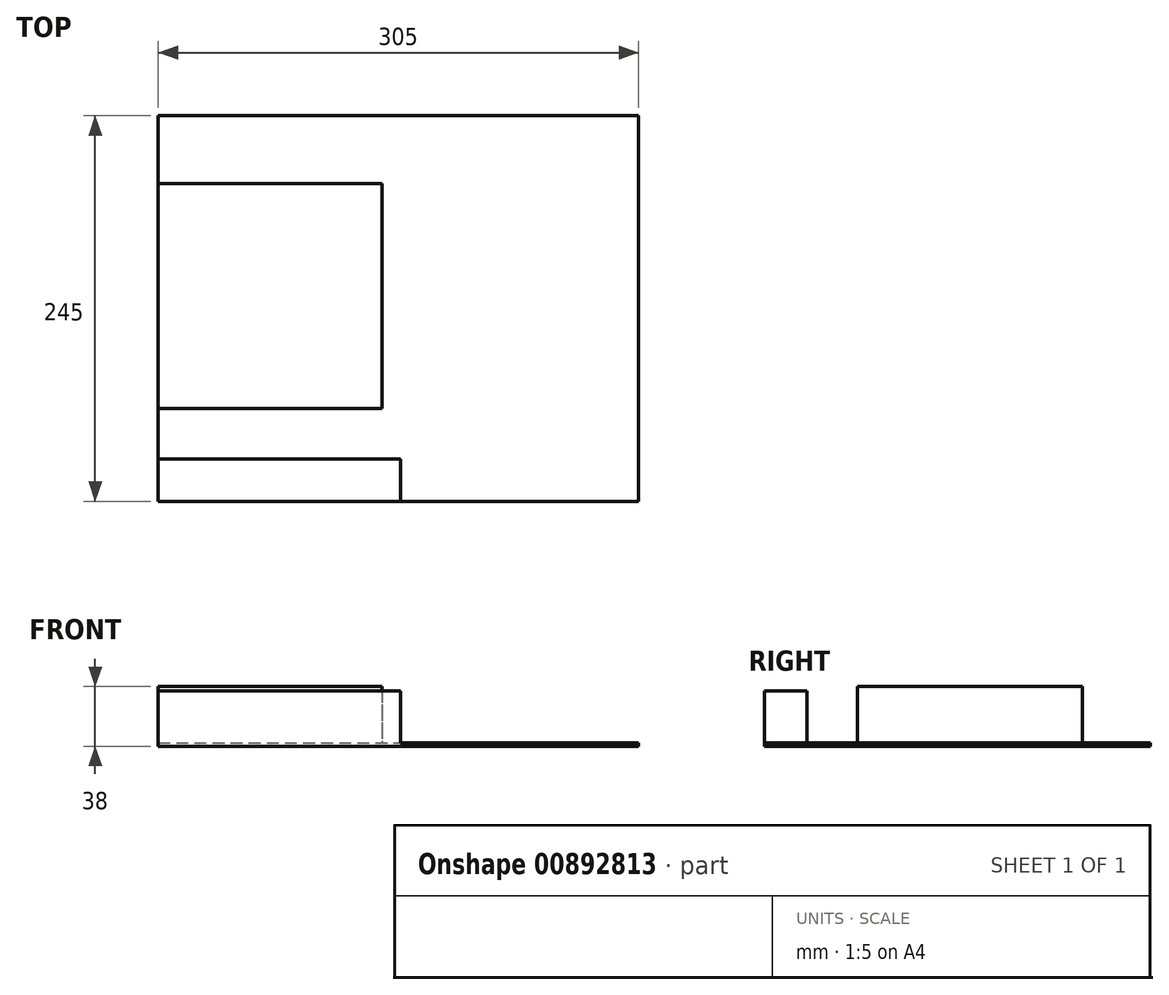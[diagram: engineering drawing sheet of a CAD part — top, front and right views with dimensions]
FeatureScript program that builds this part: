
annotation { "Feature Type Name" : "Feature", "Feature Type Description" : "" }
export const myFeature = defineFeature(function(context is Context, id is Id, definition is map)
    precondition{}
    {
        {
            var Q0;
            Q0=qCreatedBy(makeId("Top.planeOp"),FACE);
            var sketch = newSketch(context, id + "F0", { "sketchPlane" : qUnion([Q0])});
            skLineSegment(sketch, "E0.bottom", {"start": v(-152.5, 122.5) * mm, "end": v(152.5, 122.5) * mm});
            skLineSegment(sketch, "E0.top", {"start": v(-152.5, -122.5) * mm, "end": v(152.5, -122.5) * mm});
            skLineSegment(sketch, "E0.left", {"start": v(-152.5, 122.5) * mm, "end": v(-152.5, -122.5) * mm});
            skLineSegment(sketch, "E0.right", {"start": v(152.5, 122.5) * mm, "end": v(152.5, -122.5) * mm});
            skLineSegment(sketch, "E1", {"start": v(0, 146.94) * mm, "end": v(0, -146.94) * mm, "construction": true});
            skLineSegment(sketch, "E2", {"start": v(-203.7, 0) * mm, "end": v(203.7, 0) * mm, "construction": true});
            skLineSegment(sketch, "E3.bottom", {"start": v(-152.5, 79.5) * mm, "end": v(-10.5, 79.5) * mm});
            skLineSegment(sketch, "E3.top", {"start": v(-152.5, -63.5) * mm, "end": v(-10.5, -63.5) * mm});
            skLineSegment(sketch, "E3.left", {"start": v(-152.5, 79.5) * mm, "end": v(-152.5, -63.5) * mm});
            skLineSegment(sketch, "E3.right", {"start": v(-10.5, 79.5) * mm, "end": v(-10.5, -63.5) * mm});
            skLineSegment(sketch, "E4.bottom", {"start": v(-152.5, -122.5) * mm, "end": v(1.5, -122.5) * mm});
            skLineSegment(sketch, "E4.top", {"start": v(-152.5, -95.5) * mm, "end": v(1.5, -95.5) * mm});
            skLineSegment(sketch, "E4.left", {"start": v(-152.5, -122.5) * mm, "end": v(-152.5, -95.5) * mm});
            skLineSegment(sketch, "E4.right", {"start": v(1.5, -122.5) * mm, "end": v(1.5, -95.5) * mm});
            skSolve(sketch);
        }
        {
            var Q0;
            {var subQ1=sQuery(id+"F0.wireOp",EDGE,"E0.bottom");Q0=makeQuery(id+"F0.imprint","IMPRINT",FACE,{"disambiguationData":[TD([[makeQuery(id+"F0.imprint","IMPRINT",EDGE,{"derivedFrom":subQ1}),-1.0]])]});}
            extrude(context, id + "F1", {"entities" : qUnion([Q0]), "depth" : 2 * mm, "offsetDistance" : 25 * mm});
        }
        {
            var Q0;
            {var subQ0=sQuery(id+"F0.wireOp",EDGE,"E3.bottom");Q0=makeQuery(id+"F0.imprint","IMPRINT",FACE,{"disambiguationData":[TD([[makeQuery(id+"F0.imprint","IMPRINT",EDGE,{"derivedFrom":subQ0}),-1.0]])]});}
            extrude(context, id + "F2", {"entities" : qUnion([Q0]), "operationType" : NewBodyOperationType.ADD, "depth" : 38 * mm, "offsetDistance" : 25 * mm});
        }
        {
            var Q0;
            {var subQ4=sQuery(id+"F0.wireOp",EDGE,"E4.top");Q0=makeQuery(id+"F0.imprint","IMPRINT",FACE,{"disambiguationData":[TD([[makeQuery(id+"F0.imprint","IMPRINT",EDGE,{"derivedFrom":subQ4}),-1.0]])]});}
            extrude(context, id + "F3", {"entities" : qUnion([Q0]), "operationType" : NewBodyOperationType.ADD, "depth" : 35 * mm, "offsetDistance" : 25 * mm});
        }
    });
